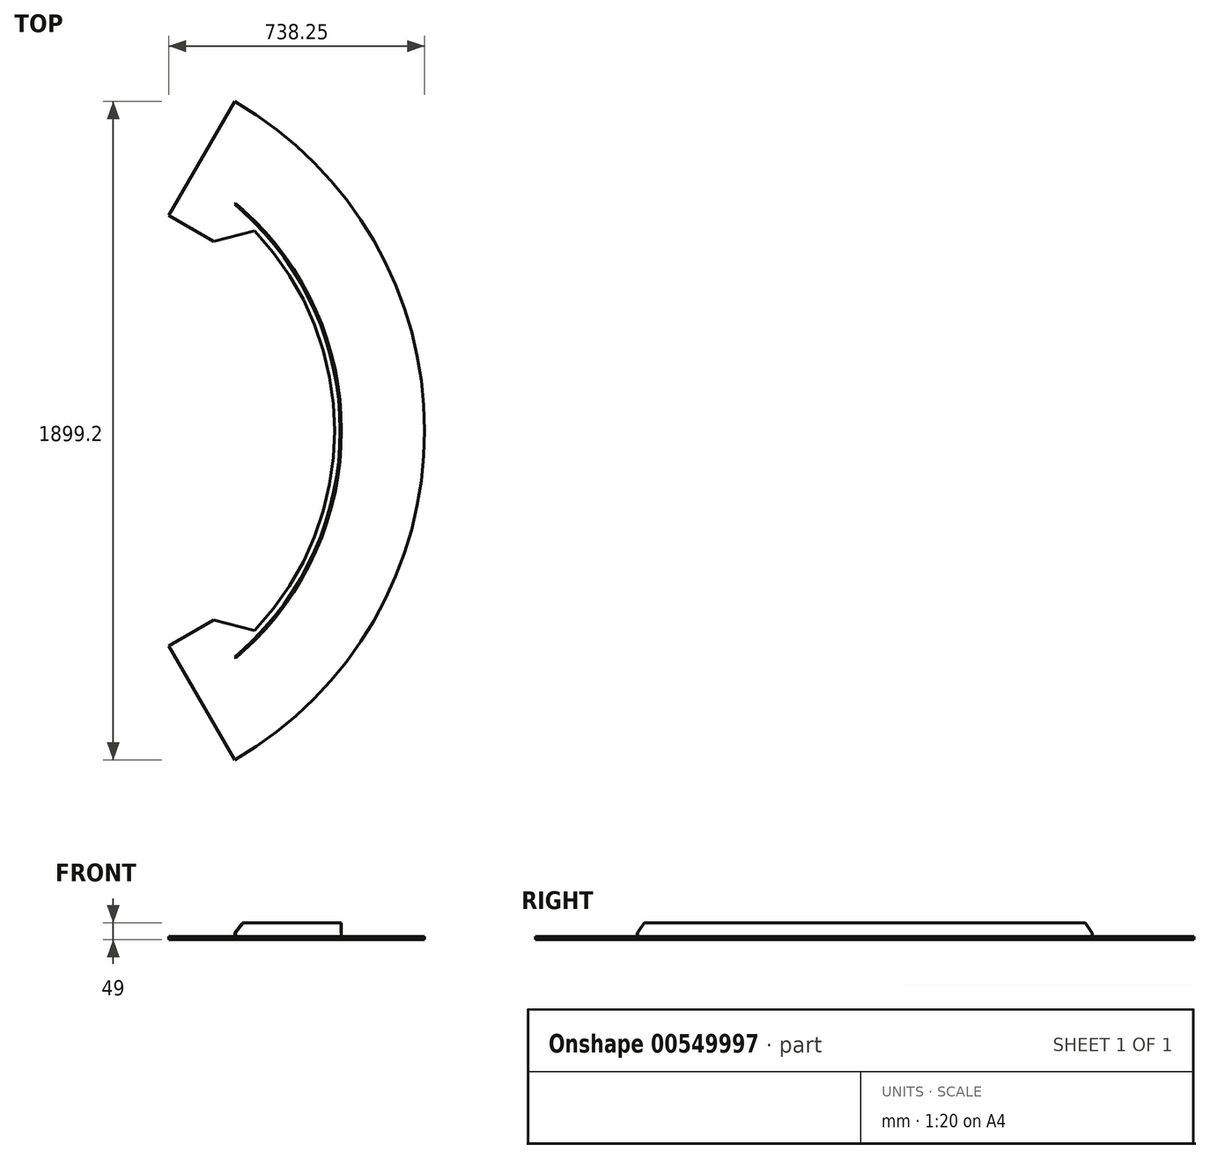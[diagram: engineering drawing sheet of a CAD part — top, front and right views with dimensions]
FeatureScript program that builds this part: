
annotation { "Feature Type Name" : "Feature", "Feature Type Description" : "" }
export const myFeature = defineFeature(function(context is Context, id is Id, definition is map)
    precondition{}
    {
        {
            var Q0;
            Q0=qCreatedBy(makeId("Top.planeOp"),FACE);
            var sketch = newSketch(context, id + "F0", { "sketchPlane" : qUnion([Q0])});
            skArc(sketch, "E0", {"start": v(548.25, -949.6) * mm, "mid": v(1096.5, 0) * mm, "end": v(548.25, 949.6) * mm});
            skArc(sketch, "E1", {"start": v(418.25, -724.43) * mm, "mid": v(836.5, 0) * mm, "end": v(418.25, 724.43) * mm});
            skLineSegment(sketch, "E2", {"start": v(418.25, -724.43) * mm, "end": v(548.25, -949.6) * mm});
            skLineSegment(sketch, "E3", {"start": v(418.25, 724.43) * mm, "end": v(548.25, 949.6) * mm});
            skSolve(sketch);
        }
        {
            var Q0;
            Q0=makeQuery(id+"F0.imprint","IMPRINT",FACE,{"disambiguationData":[TD([[makeQuery(id+"F0.imprint","IMPRINT",EDGE,{"derivedFrom":sQuery(id+"F0.wireOp",EDGE,"E0")}),1.0]])]});
            extrude(context, id + "F1", {"entities" : qUnion([Q0]), "depth" : 9 * mm, "offsetDistance" : 25 * mm});
        }
        {
            var Q0;
            Q0=makeQuery(id+"F1.opExtrude","CAP_FACE",FACE,{"disambiguationData":[OSD([sQuery(id+"F0.wireOp",EDGE,"E0"),sQuery(id+"F0.wireOp",EDGE,"E1")])],"isStart":false});
            var sketch = newSketch(context, id + "F2", { "sketchPlane" : qUnion([Q0])});
            skArc(sketch, "E4.0", {"start": v(550.55, -656.12) * mm, "mid": v(856.5, 0) * mm, "end": v(550.55, 656.12) * mm});
            skArc(sketch, "E5.0", {"start": v(547.98, -653.05) * mm, "mid": v(852.5, 0) * mm, "end": v(547.98, 653.05) * mm});
            skLineSegment(sketch, "E6", {"start": v(0, 0) * mm, "end": v(1536.58, 0) * mm, "construction": true});
            skLineSegment(sketch, "E7", {"start": v(547.98, 653.05) * mm, "end": v(550.55, 656.12) * mm});
            skLineSegment(sketch, "E8", {"start": v(547.98, -653.05) * mm, "end": v(550.55, -656.12) * mm});
            skSolve(sketch);
        }
        {
            var Q0;
            Q0 = qSketchRegion(id + "F2", true);
            extrude(context, id + "F3", {"entities" : qUnion([Q0]), "operationType" : NewBodyOperationType.ADD, "depth" : 40 * mm, "offsetDistance" : 25 * mm});
        }
        {
            var Q0;
            Q0=makeQuery(id+"F0.imprint","IMPRINT",FACE,{"disambiguationData":[TD([[makeQuery(id+"F0.imprint","IMPRINT",EDGE,{"derivedFrom":sQuery(id+"F0.wireOp",EDGE,"E0")}),1.0]])]});
            var sketch = newSketch(context, id + "F4", { "sketchPlane" : qUnion([Q0])});
            skLineSegment(sketch, "E9", {"start": v(418.25, -724.43) * mm, "end": v(358.25, -620.5) * mm});
            skLineSegment(sketch, "E10", {"start": v(358.25, -620.5) * mm, "end": v(488.15, -545.5) * mm});
            skLineSegment(sketch, "E11", {"start": v(488.15, -545.5) * mm, "end": v(605.65, -577) * mm});
            skArc(sketch, "E12.0", {"start": v(418.25, -724.43) * mm, "mid": v(517.23, -657.42) * mm, "end": v(605.65, -577) * mm});
            skPoint(sketch, "E13.orphan", {"position": v(418.25, 724.43) * mm});
            skSolve(sketch);
        }
        {
            var Q0;
            Q0=makeQuery(id+"F4.imprint","IMPRINT",FACE,{"disambiguationData":[TD([[makeQuery(id+"F4.imprint","IMPRINT",EDGE,{"derivedFrom":sQuery(id+"F4.wireOp",EDGE,"E9")}),-1.0]])]});
            extrude(context, id + "F5", {"entities" : qUnion([Q0]), "depth" : 9 * mm, "offsetDistance" : 25 * mm});
        }
        {
            var Q0;
            Q0=makeQuery(id+"F5.opExtrude","SWEPT_BODY",BODY,{"disambiguationData":[OSD([sQuery(id+"F4.wireOp",EDGE,"E9"),sQuery(id+"F4.wireOp",EDGE,"E10"),sQuery(id+"F4.wireOp",EDGE,"E11"),sQuery(id+"F4.wireOp",EDGE,"E12.0")])]});
            var Q1;
            Q1=qCreatedBy(makeId("Front.planeOp"),FACE);
            mirror(context, id + "F6", {"operationType" : NewBodyOperationType.ADD, "entities" : qUnion([Q0]), "mirrorPlane" : qUnion([Q1])});
        }
        {
            var Q0;
            Q0=makeQuery(id+"F3.opExtrude","CAP_EDGE",EDGE,{"disambiguationData":[OSD([sQuery(id+"F2.wireOp",EDGE,"E8")])],"isStart":false});
            var Q1;
            Q1=makeQuery(id+"F3.opExtrude","CAP_EDGE",EDGE,{"disambiguationData":[OSD([sQuery(id+"F2.wireOp",EDGE,"E7")])],"isStart":false});
            chamfer(context, id + "F7", {"entities" : qUnion([Q0, Q1]), "chamferType" : ChamferType.OFFSET_ANGLE, "width" : 30 * mm, "oppositeDirection" : false, "angle" : 45 * degree, "tangentPropagation" : true});
        }
    });
